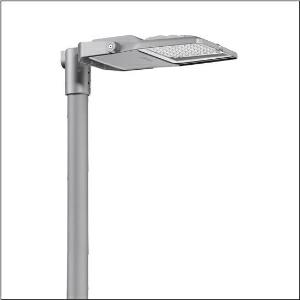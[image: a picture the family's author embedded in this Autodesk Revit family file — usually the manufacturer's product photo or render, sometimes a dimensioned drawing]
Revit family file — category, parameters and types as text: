
# Revit family: floodlight_fl_21_iq_mini___pl43_5xa7772d2a3a_1f0e
name_source: partatom
category: Lighting Fixtures
units: mm (PartAtom-declared; Revit-internal decimal feet)

## family parameters
Cut with Voids When Loaded = No
Host = Face
Light Source = No
Part Type = Normal
Room Calculation Point = No
Round Connector Dimension = Use Diameter
Shared = No

## types (1)
- --- (1 x LED, 18290 lm, 143 W, 3000K)
    Apparent Load = 143 VA
    CIE Flux Codes = 27 78 99 100 100
    Color Rendering = 70
    Color Temperature = 3000K
    Default Elevation = 1800 mm
    Description = Floodlight FL 21 iQ mini, floodlight, primary light control with lens, of PMMA, primary optical cover: protective disc, of toughened safety glass, transparent, light distribution: PL43, light emission: direct distribution, installation type: surface-mounted, lamps: LED, High Power LED, rated values: 18.290lm | 143W | 127,9lm/W (begin service life); end service life: 18.290lm | 151,6W; at 50% lumin. flux: 9.145lm | 60,6W | 150,9lm/W, colour temperature: 3000K, colour rendering: CRI > 70, light colour: 730, light setting 1 begin service life: 100% | 18.290lm | 143W | 127,9lm/W | 3.000K, light setting 1 end service life: 151,6W, further light settings possible, control: pre-setting: linear dimming characteristic, Auto-Match, Temp-Guard, Night-Set, Smart-Wire, Desk-Remote (wireless, voltage-free reading and setting of iQ features in the workshop via application-optimized NFC function/RFID function), optimised constant luminous flux control (CLO 2.0), Light-Fading, Lumen-Switch, with terminal, 6-pole, mains connection: 220..240V, AC, 50/60Hz, luminaire housing, of diecast aluminium, powder-coated, SITECO metallic grey (DB 702S), corrosivity category C5 mid according to DIN EN ISO 12944suitable for swimming poolschlorine-resistant, sealing non-destructively replaceable, please order mast flange separately, mast bracket, of steel, galvanised, powder-coated, protection rating (complete): IP66, insulation class (complete): insulation class II (safety insulation), certification: CE, ENEC, VDE, protection symbol: D, impact resistance: IK08, permissible operating ambient temperature: -40..+40°C, permissible operating ambient temperature for outdoor applications: -40..+50°C, standard: DIN EN 12944, LABS conformity tested according to VDMA 24364:2018-05, packaging unit: 1 piece

Light Distribution: PL43
    Height = 70 mm
    Lamp = 1 x LED
    Lamp Light Flux = 18290 lm
    Lamp Power = 143 W
    Lamp count = 1
    Length = 485 mm
    Luminous efficacy = 128 lm/W
    Manufacturer = Siteco
    ModVariant = No
    Model = 5XA7772D2A3A
    Mounting Place = Pole
    Mounting Type = Pole annexe
    Number of Poles = 1
    OnlyDefault = Yes
    Power Factor = 1
    Product Name = Floodlight FL 21 iQ mini | PL43
    Product group = floodlight | pylon annexe
    ProductGroupID = 6201
    Protection Class = Protection class II
    Protection Degree = IP 66
    RLX_Detail_Level = 1
    RLX_Emergency_Light_Flux = 0 lm
    RLX_Emergency_Type = 0
    RLX_Emergency_Type_DB = No
    RlxData = <blob elided: 101793 chars, md5=514e1c70>
    Socket = socket
    Standby Power = 0 W
    System Light Flux = 18290 lm
    System Power = 143 W
    Type Comments = factory setting: luminous flux: 100 % | dim-lin: 254 | 730 mA
    Type Image = l_1007125.jpg
    URL = http://relux.com
    VarID = @adj_162641
    Voltage = 0 V
    Weight = 0.00 kg
    Width = 337 mm

## geometry (parser evidence)
native form markers: Blend x4, Sweep x13
no freeform markers — native parametric forms only
